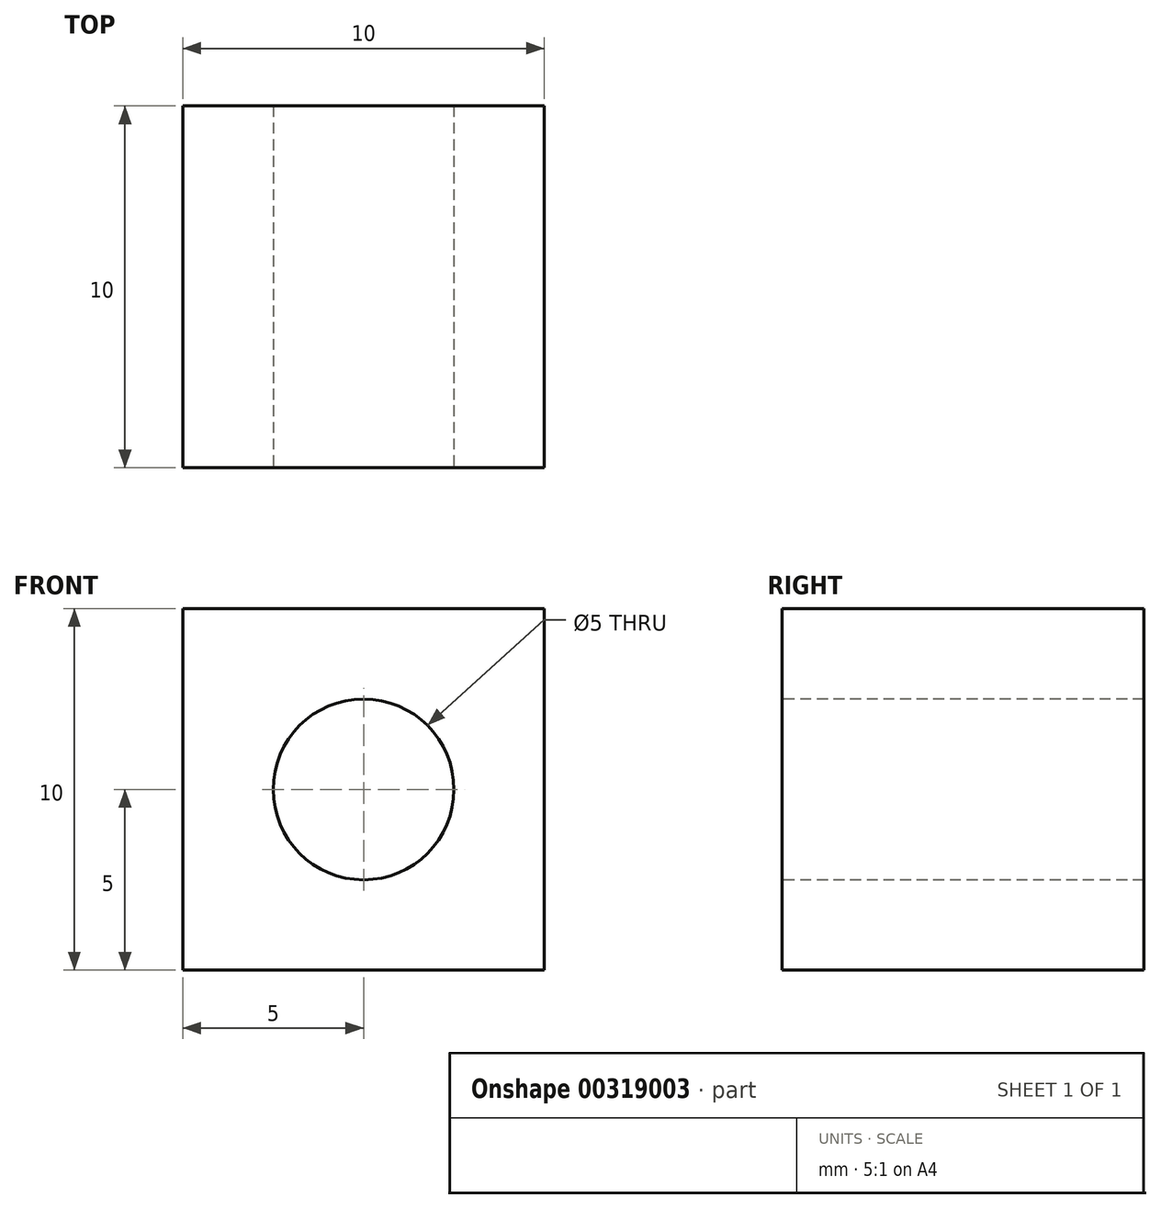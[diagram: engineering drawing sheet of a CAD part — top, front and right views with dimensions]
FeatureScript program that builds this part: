
annotation { "Feature Type Name" : "Feature", "Feature Type Description" : "" }
export const myFeature = defineFeature(function(context is Context, id is Id, definition is map)
    precondition{}
    {
        {
            var Q0;
            Q0=qCreatedBy(makeId("Front.planeOp"),FACE);
            var sketch = newSketch(context, id + "F0", { "sketchPlane" : qUnion([Q0])});
            skLineSegment(sketch, "E0", {"start": v(-5, 5) * mm, "end": v(5, 5) * mm});
            skLineSegment(sketch, "E1", {"start": v(5, 5) * mm, "end": v(5, -5) * mm});
            skLineSegment(sketch, "E2", {"start": v(5, -5) * mm, "end": v(-5, -5) * mm});
            skLineSegment(sketch, "E3", {"start": v(-5, -5) * mm, "end": v(-5, 5) * mm});
            skPoint(sketch, "E4", {"position": v(0, 5) * mm});
            skPoint(sketch, "E5", {"position": v(5, 0) * mm});
            skSolve(sketch);
        }
        {
            var Q0;
            Q0=makeQuery(id+"F0.imprint","IMPRINT",FACE,{"disambiguationData":[TD([[makeQuery(id+"F0.imprint","IMPRINT",EDGE,{"derivedFrom":sQuery(id+"F0.wireOp",EDGE,"E0")}),-1.0]])]});
            extrude(context, id + "F1", {"entities" : qUnion([Q0]), "depth" : 10 * mm, "symmetric" : true});
        }
        {
            var Q0;
            Q0=makeQuery(id+"F1.opExtrude","CAP_FACE",FACE,{"disambiguationData":[OSD([sQuery(id+"F0.wireOp",EDGE,"E0"),sQuery(id+"F0.wireOp",EDGE,"E1"),sQuery(id+"F0.wireOp",EDGE,"E2"),sQuery(id+"F0.wireOp",EDGE,"E3")])],"isStart":false});
            var sketch = newSketch(context, id + "F2", { "sketchPlane" : qUnion([Q0])});
            skCircle(sketch, "E6", {"center": v(0, 0) * mm, "radius": 2.5 * mm});
            skSolve(sketch);
        }
        {
            var Q0;
            Q0 = qSketchRegion(id + "F2", true);
            extrude(context, id + "F3", {"entities" : qUnion([Q0]), "operationType" : NewBodyOperationType.REMOVE, "endBound" : BoundingType.THROUGH_ALL, "oppositeDirection" : true, "depth" : 25 * mm});
        }
    });
